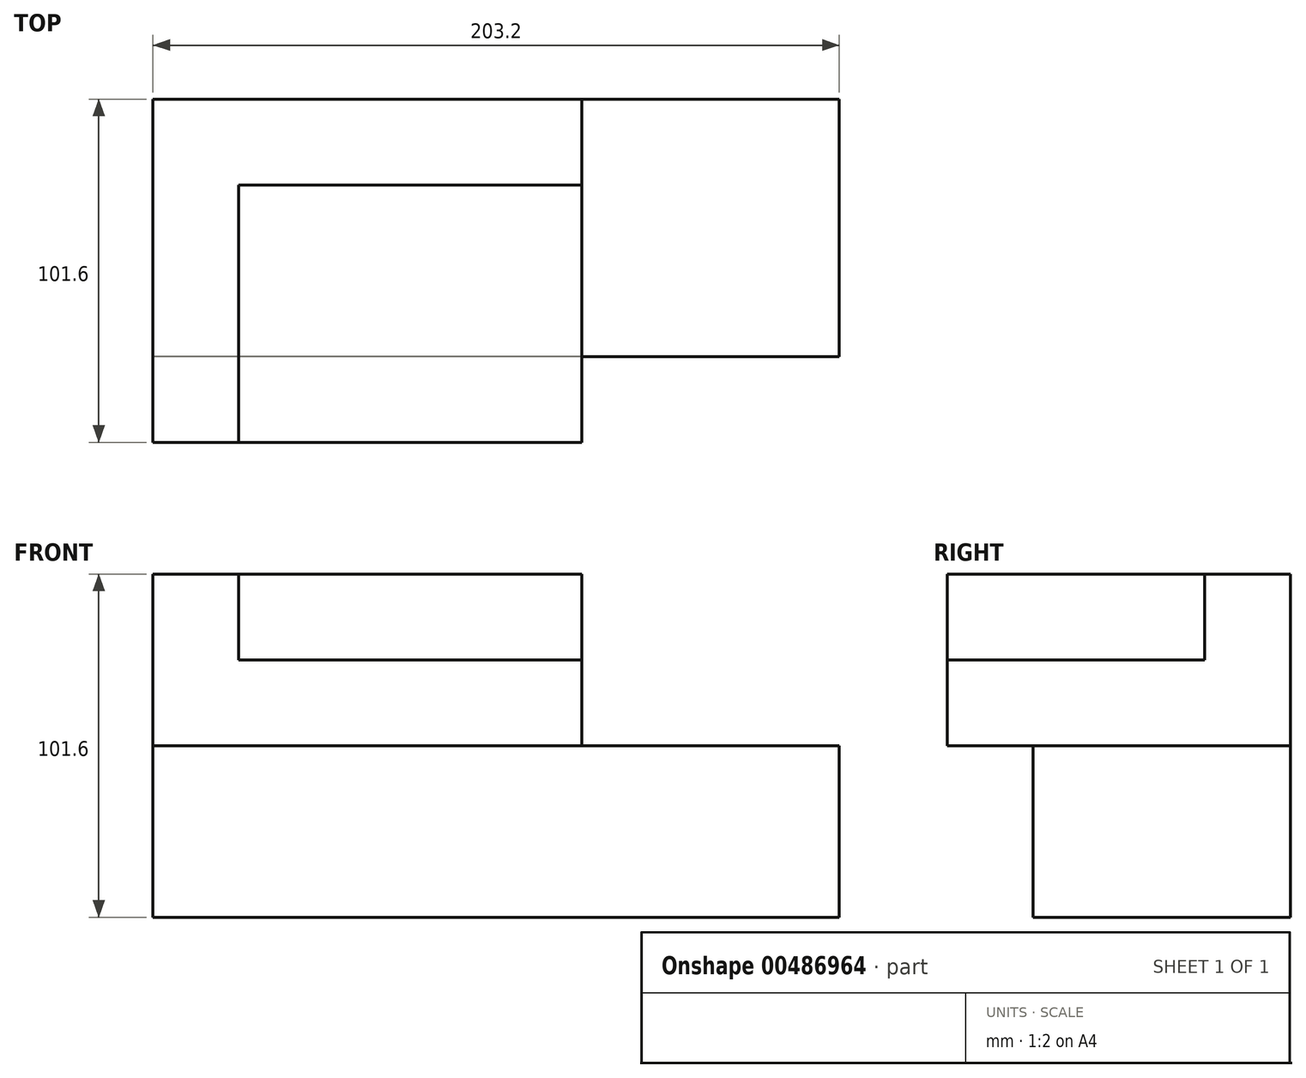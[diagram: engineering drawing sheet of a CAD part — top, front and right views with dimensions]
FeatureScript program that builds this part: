
annotation { "Feature Type Name" : "Feature", "Feature Type Description" : "" }
export const myFeature = defineFeature(function(context is Context, id is Id, definition is map)
    precondition{}
    {
        {
            var Q0;
            Q0=qCreatedBy(makeId("Front.planeOp"),FACE);
            var sketch = newSketch(context, id + "F0", { "sketchPlane" : qUnion([Q0])});
            skLineSegment(sketch, "E0.bottom", {"start": v(0, 0) * mm, "end": v(-203.2, 0) * mm});
            skLineSegment(sketch, "E0.top", {"start": v(0, 76.2) * mm, "end": v(-203.2, 76.2) * mm});
            skLineSegment(sketch, "E0.left", {"start": v(0, 0) * mm, "end": v(0, 76.2) * mm});
            skLineSegment(sketch, "E0.right", {"start": v(-203.2, 0) * mm, "end": v(-203.2, 76.2) * mm});
            skSolve(sketch);
        }
        {
            var Q0;
            Q0=makeQuery(id+"F0.imprint","IMPRINT",FACE,{"disambiguationData":[TD([[makeQuery(id+"F0.imprint","IMPRINT",EDGE,{"derivedFrom":sQuery(id+"F0.wireOp",EDGE,"E0.bottom")}),-1.0]])]});
            extrude(context, id + "F1", {"entities" : qUnion([Q0]), "depth" : 50.8 * mm});
        }
        {
            var Q0;
            Q0=makeQuery(id+"F1.opExtrude","CAP_FACE",FACE,{"disambiguationData":[OSD([sQuery(id+"F0.wireOp",EDGE,"E0.bottom"),sQuery(id+"F0.wireOp",EDGE,"E0.top"),sQuery(id+"F0.wireOp",EDGE,"E0.left"),sQuery(id+"F0.wireOp",EDGE,"E0.right")])],"isStart":false});
            var sketch = newSketch(context, id + "F2", { "sketchPlane" : qUnion([Q0])});
            skLineSegment(sketch, "E1.bottom", {"start": v(-203.2, 76.2) * mm, "end": v(-76.2, 76.2) * mm});
            skLineSegment(sketch, "E1.top", {"start": v(-203.2, -25.4) * mm, "end": v(-76.2, -25.4) * mm});
            skLineSegment(sketch, "E1.left", {"start": v(-203.2, 76.2) * mm, "end": v(-203.2, -25.4) * mm});
            skLineSegment(sketch, "E1.right", {"start": v(-76.2, 76.2) * mm, "end": v(-76.2, -25.4) * mm});
            skSolve(sketch);
        }
        {
            var Q0;
            {var subQ0=sQuery(id+"F2.wireOp",EDGE,"E1.bottom");Q0=makeQuery(id+"F2.imprint","IMPRINT",FACE,{"disambiguationData":[TD([[makeQuery(id+"F2.imprint","IMPRINT",EDGE,{"derivedFrom":subQ0}),1.0]])]});}
            var Q1;
            {var subQ0=sQuery(id+"F2.wireOp",EDGE,"E1.top");Q1=makeQuery(id+"F2.imprint","IMPRINT",FACE,{"disambiguationData":[TD([[makeQuery(id+"F2.imprint","IMPRINT",EDGE,{"derivedFrom":subQ0}),1.0]])]});}
            extrude(context, id + "F3", {"entities" : qUnion([Q0, Q1]), "operationType" : NewBodyOperationType.ADD, "depth" : 50.8 * mm});
        }
        {
            var Q0;
            Q0=makeQuery(id+"F3.opExtrude","CAP_FACE",FACE,{"disambiguationData":[OSD([sQuery(id+"F2.wireOp",EDGE,"E1.bottom"),sQuery(id+"F2.wireOp",EDGE,"E1.top"),sQuery(id+"F2.wireOp",EDGE,"E1.left"),sQuery(id+"F2.wireOp",EDGE,"E1.right")])],"isStart":false});
            var sketch = newSketch(context, id + "F4", { "sketchPlane" : qUnion([Q0])});
            skLineSegment(sketch, "E2.bottom", {"start": v(-76.2, -25.4) * mm, "end": v(-177.8, -25.4) * mm});
            skLineSegment(sketch, "E2.top", {"start": v(-76.2, 50.8) * mm, "end": v(-177.8, 50.8) * mm});
            skLineSegment(sketch, "E2.left", {"start": v(-76.2, -25.4) * mm, "end": v(-76.2, 50.8) * mm});
            skLineSegment(sketch, "E2.right", {"start": v(-177.8, -25.4) * mm, "end": v(-177.8, 50.8) * mm});
            skSolve(sketch);
        }
        {
            var Q0;
            Q0=makeQuery(id+"F4.imprint","IMPRINT",FACE,{"disambiguationData":[TD([[makeQuery(id+"F4.imprint","IMPRINT",EDGE,{"derivedFrom":sQuery(id+"F4.wireOp",EDGE,"E2.bottom")}),1.0]])]});
            extrude(context, id + "F5", {"entities" : qUnion([Q0]), "operationType" : NewBodyOperationType.REMOVE, "oppositeDirection" : true, "depth" : 25.4 * mm});
        }
        {
            var Q0;
            Q0=makeQuery(id+"F1.opExtrude","SWEPT_BODY",BODY,{"disambiguationData":[OSD([sQuery(id+"F0.wireOp",EDGE,"E0.bottom"),sQuery(id+"F0.wireOp",EDGE,"E0.top"),sQuery(id+"F0.wireOp",EDGE,"E0.left"),sQuery(id+"F0.wireOp",EDGE,"E0.right")])]});
            var Q1;
            Q1=makeQuery(id+"F1.opExtrude","CAP_EDGE",EDGE,{"disambiguationData":[OSD([sQuery(id+"F0.wireOp",EDGE,"E0.bottom")])],"isStart":true});
            transform(context, id + "F6", {"entities" : qUnion([Q0]), "transformType" : TransformType.ROTATION, "transformAxis" : qUnion([Q1]), "angle" : 90 * degree, "makeCopy" : false});
        }
    });
